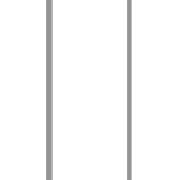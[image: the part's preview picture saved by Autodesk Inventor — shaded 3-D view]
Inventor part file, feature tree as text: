
AUTODESK INVENTOR PART (.ipt)
format: ipt  version: 2021 (Build 250183000, 183)  size: 149,504 bytes
history: native  units: in
note: dims shown in document units (in); Inventor stores cm internally (conversion verified against a paired STEP export)
features: plane x5, sketch x5, other x4, hole x1, extrude x1, boolean_combine x1
ambient origin geometry x8: Origin, YZ Plane, XZ Plane, XY Plane, X Axis, Y Axis, Z Axis, Center Point
bodies: Solid1 (feature_tree), Body (feature_tree), Solid2 (feature_tree)
feature tree (17):
  other  "Driven Length"
  other  "Frame Generator"
  plane  "Work Plane3"
  other  "Start Plane"
  other  "End Plane"
  hole  "Hole2"  [1 undecoded]
  plane  "Work Plane7"
  plane  "Work Plane8"
  plane  "Work Plane9"
  extrude  "Extrusion3"  Depth=0.0625in
  boolean_combine  "Combine1"
  sketch  "Sketch"  dims[d17=2.0in d18=0.12in d19=0.0in d22=1.5in d23=0.4375in d24=0.75in d25=0.635in d26=0.25in d27=0.5635in d28=1.0in d29=0.8108in d32=90.0deg d21=2.0in d34=0.12in d35=0.0in d8=0.5in d9=0.0344in d10=0.5in d11=0.0344in]
  sketch  "Sketch5"  dims[d0=1.5in d1=1.0in]
  sketch  "Sketch8"  dims[d2=0.0625in d3=0.0625in]
  plane  "Work Plane6"
  sketch  "Sketch9"  dims[d4=2.0in]
  sketch  "Sketch10"  dims[d16=-0.0in]
note: 1 required parameter value undecoded (feature->parameter linkage not recoverable at this tier; creation-order binding heuristic only, values carry confidence <= 0.55)
